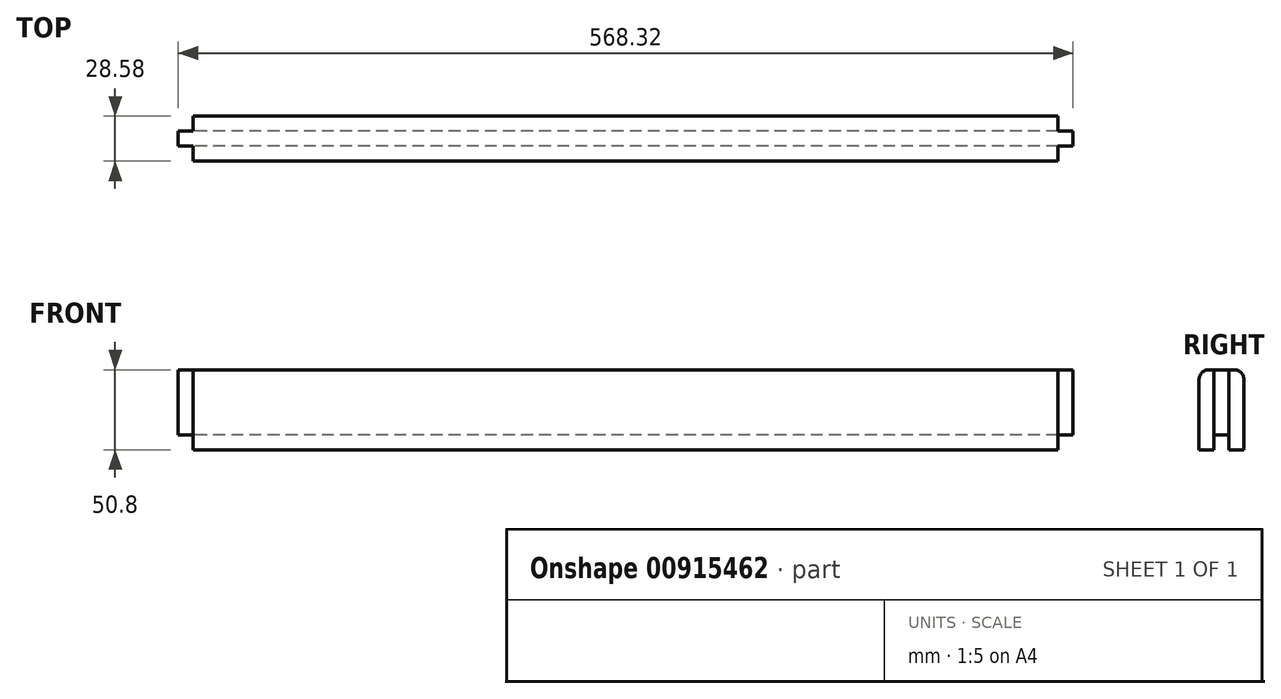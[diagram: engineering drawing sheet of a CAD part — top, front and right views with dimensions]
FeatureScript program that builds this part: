
annotation { "Feature Type Name" : "Feature", "Feature Type Description" : "" }
export const myFeature = defineFeature(function(context is Context, id is Id, definition is map)
    precondition{}
    {
        {
            var Q0;
            Q0=qCreatedBy(makeId("Right.planeOp"),FACE);
            var sketch = newSketch(context, id + "F0", { "sketchPlane" : qUnion([Q0])});
            skLineSegment(sketch, "E0", {"start": v(0, 0) * mm, "end": v(0, 50.8) * mm});
            skLineSegment(sketch, "E1", {"start": v(0, 50.8) * mm, "end": v(28.58, 50.8) * mm});
            skLineSegment(sketch, "E2", {"start": v(28.58, 50.8) * mm, "end": v(28.58, 0) * mm});
            skLineSegment(sketch, "E3", {"start": v(28.58, 0) * mm, "end": v(19.05, 0) * mm});
            skLineSegment(sketch, "E4", {"start": v(19.05, 0) * mm, "end": v(19.05, 9.53) * mm});
            skLineSegment(sketch, "E5", {"start": v(19.05, 9.53) * mm, "end": v(9.53, 9.53) * mm});
            skLineSegment(sketch, "E6", {"start": v(9.53, 9.53) * mm, "end": v(9.53, 0) * mm});
            skLineSegment(sketch, "E7", {"start": v(9.53, 0) * mm, "end": v(0, 0) * mm});
            skSolve(sketch);
        }
        {
            var Q0;
            Q0=makeQuery(id+"F0.imprint","IMPRINT",FACE,{"disambiguationData":[TD([[makeQuery(id+"F0.imprint","IMPRINT",EDGE,{"derivedFrom":sQuery(id+"F0.wireOp",EDGE,"E0")}),-1.0]])]});
            extrude(context, id + "F1", {"entities" : qUnion([Q0]), "depth" : 568.32 * mm, "offsetDistance" : 25.4 * mm});
        }
        {
            var Q0;
            Q0=makeQuery(id+"F1.opExtrude","SWEPT_FACE",FACE,{"disambiguationData":[OSD([sQuery(id+"F0.wireOp",EDGE,"E1")])]});
            var sketch = newSketch(context, id + "F2", { "sketchPlane" : qUnion([Q0])});
            skLineSegment(sketch, "E8.bottom", {"start": v(0, 28.58) * mm, "end": v(9.53, 28.58) * mm});
            skLineSegment(sketch, "E8.top", {"start": v(0, 19.05) * mm, "end": v(9.53, 19.05) * mm});
            skLineSegment(sketch, "E8.left", {"start": v(0, 28.58) * mm, "end": v(0, 19.05) * mm});
            skLineSegment(sketch, "E8.right", {"start": v(9.53, 28.58) * mm, "end": v(9.53, 19.05) * mm});
            skLineSegment(sketch, "E9.bottom", {"start": v(0, 0) * mm, "end": v(9.53, 0) * mm});
            skLineSegment(sketch, "E9.top", {"start": v(0, 9.53) * mm, "end": v(9.53, 9.53) * mm});
            skLineSegment(sketch, "E9.left", {"start": v(0, 0) * mm, "end": v(0, 9.53) * mm});
            skLineSegment(sketch, "E9.right", {"start": v(9.53, 0) * mm, "end": v(9.52, 9.53) * mm});
            skLineSegment(sketch, "E10.bottom", {"start": v(568.33, 28.58) * mm, "end": v(558.8, 28.58) * mm});
            skLineSegment(sketch, "E10.top", {"start": v(568.33, 19.05) * mm, "end": v(558.8, 19.05) * mm});
            skLineSegment(sketch, "E10.left", {"start": v(568.33, 28.58) * mm, "end": v(568.33, 19.05) * mm});
            skLineSegment(sketch, "E10.right", {"start": v(558.8, 28.58) * mm, "end": v(558.8, 19.05) * mm});
            skLineSegment(sketch, "E11.bottom", {"start": v(568.33, 0) * mm, "end": v(558.8, 0) * mm});
            skLineSegment(sketch, "E11.top", {"start": v(568.33, 9.53) * mm, "end": v(558.8, 9.53) * mm});
            skLineSegment(sketch, "E11.left", {"start": v(568.33, 0) * mm, "end": v(568.33, 9.53) * mm});
            skLineSegment(sketch, "E11.right", {"start": v(558.8, 0) * mm, "end": v(558.8, 9.53) * mm});
            skSolve(sketch);
        }
        {
            var Q0;
            Q0=makeQuery(id+"F2.imprint","IMPRINT",FACE,{"disambiguationData":[TD([[makeQuery(id+"F2.imprint","IMPRINT",EDGE,{"derivedFrom":sQuery(id+"F2.wireOp",EDGE,"E8.bottom")}),1.0]])]});
            var Q1;
            Q1=makeQuery(id+"F2.imprint","IMPRINT",FACE,{"disambiguationData":[TD([[makeQuery(id+"F2.imprint","IMPRINT",EDGE,{"derivedFrom":sQuery(id+"F2.wireOp",EDGE,"E9.bottom")}),-1.0]])]});
            var Q2;
            Q2=makeQuery(id+"F2.imprint","IMPRINT",FACE,{"disambiguationData":[TD([[makeQuery(id+"F2.imprint","IMPRINT",EDGE,{"derivedFrom":sQuery(id+"F2.wireOp",EDGE,"E10.bottom")}),1.0]])]});
            var Q3;
            Q3=makeQuery(id+"F2.imprint","IMPRINT",FACE,{"disambiguationData":[TD([[makeQuery(id+"F2.imprint","IMPRINT",EDGE,{"derivedFrom":sQuery(id+"F2.wireOp",EDGE,"E11.bottom")}),-1.0]])]});
            extrude(context, id + "F3", {"entities" : qUnion([Q0, Q1, Q2, Q3]), "operationType" : NewBodyOperationType.REMOVE, "oppositeDirection" : true, "depth" : 50.8 * mm, "offsetDistance" : 25.4 * mm});
        }
        {
            var Q0;
            Q0=makeQuery(id+"F1.opExtrude","SWEPT_EDGE",EDGE,{"disambiguationData":[OSD([sQuery(id+"F0.wireOp",EDGE,"E0"),sQuery(id+"F0.wireOp",EDGE,"E1")])]});
            var Q1;
            Q1=makeQuery(id+"F1.opExtrude","SWEPT_EDGE",EDGE,{"disambiguationData":[OSD([sQuery(id+"F0.wireOp",EDGE,"E1"),sQuery(id+"F0.wireOp",EDGE,"E2")])]});
            fillet(context, id + "F4", {"entities" : qUnion([Q0, Q1]), "radius" : 6.35 * mm, "tangentPropagation" : true, "allowEdgeOverflow" : false});
        }
    });
